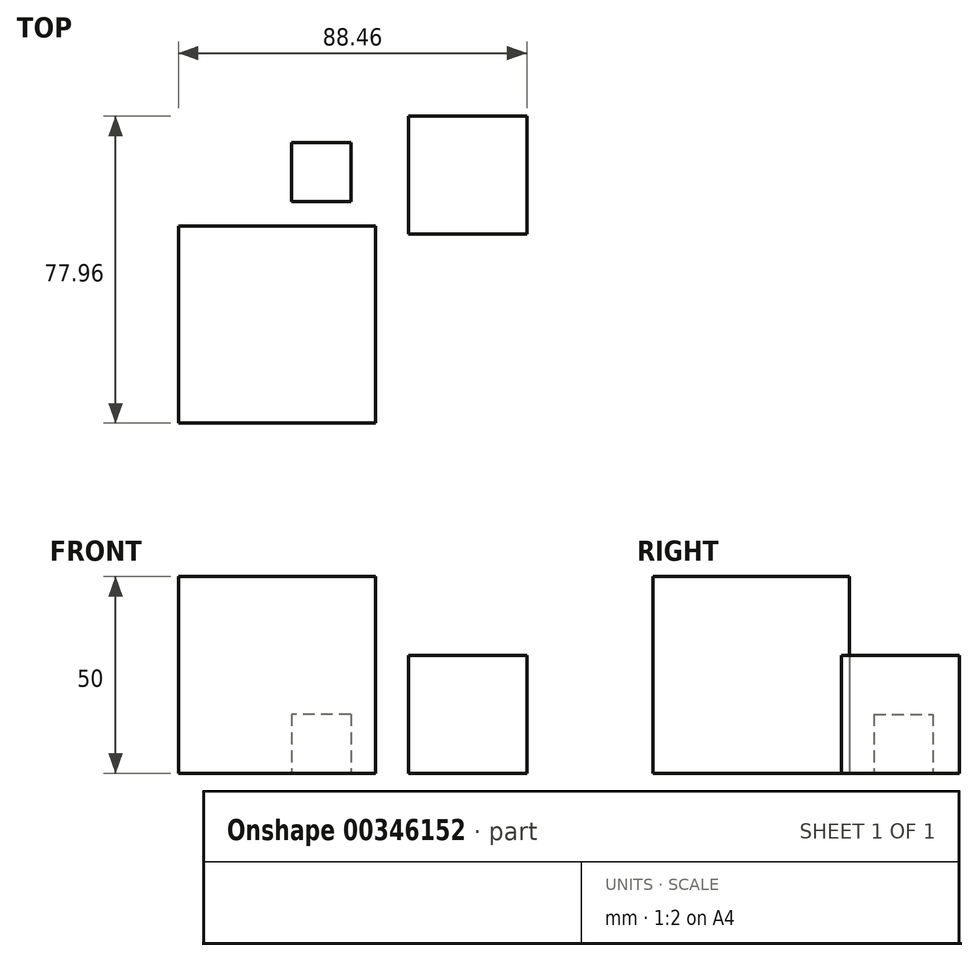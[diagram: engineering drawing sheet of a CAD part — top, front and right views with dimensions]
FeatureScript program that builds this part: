
annotation { "Feature Type Name" : "Feature", "Feature Type Description" : "" }
export const myFeature = defineFeature(function(context is Context, id is Id, definition is map)
    precondition{}
    {
        {
            assignVariable(context, id + "F0", {"name" : "a", "anyValue" : 15});
        }
        {
            assignVariable(context, id + "F1", {"name" : "b", "anyValue" : 30});
        }
        {
            assignVariable(context, id + "F2", {"name" : "c", "anyValue" : 50});
        }
        {
            var Q0;
            Q0=qCreatedBy(makeId("Top.planeOp"),FACE);
            var sketch = newSketch(context, id + "F3", { "sketchPlane" : qUnion([Q0])});
            skLineSegment(sketch, "E0.bottom", {"start": v(-35.32, 58.54) * mm, "end": v(-50.32, 58.54) * mm});
            skLineSegment(sketch, "E0.top", {"start": v(-35.32, 73.54) * mm, "end": v(-50.32, 73.54) * mm});
            skLineSegment(sketch, "E0.left", {"start": v(-35.32, 58.54) * mm, "end": v(-35.32, 73.54) * mm});
            skLineSegment(sketch, "E0.right", {"start": v(-50.32, 58.54) * mm, "end": v(-50.32, 73.54) * mm});
            skLineSegment(sketch, "E1.bottom", {"start": v(-20.62, 50.29) * mm, "end": v(9.38, 50.29) * mm});
            skLineSegment(sketch, "E1.top", {"start": v(-20.62, 80.29) * mm, "end": v(9.38, 80.29) * mm});
            skLineSegment(sketch, "E1.left", {"start": v(-20.62, 50.29) * mm, "end": v(-20.62, 80.29) * mm});
            skLineSegment(sketch, "E1.right", {"start": v(9.38, 50.29) * mm, "end": v(9.38, 80.29) * mm});
            skLineSegment(sketch, "E2.bottom", {"start": v(-79.08, 2.33) * mm, "end": v(-29.08, 2.33) * mm});
            skLineSegment(sketch, "E2.top", {"start": v(-79.08, 52.33) * mm, "end": v(-29.08, 52.33) * mm});
            skLineSegment(sketch, "E2.left", {"start": v(-79.08, 2.33) * mm, "end": v(-79.08, 52.33) * mm});
            skLineSegment(sketch, "E2.right", {"start": v(-29.08, 2.33) * mm, "end": v(-29.08, 52.33) * mm});
            skSolve(sketch);
        }
        {
            var Q0;
            Q0=makeQuery(id+"F3.imprint","IMPRINT",FACE,{"disambiguationData":[TD([[makeQuery(id+"F3.imprint","IMPRINT",EDGE,{"derivedFrom":sQuery(id+"F3.wireOp",EDGE,"E0.bottom")}),-1.0]])]});
            extrude(context, id + "F4", {"entities" : qUnion([Q0]), "depth" : (getVariable(context, 'a')) * mm});
        }
        {
            var Q0;
            Q0=makeQuery(id+"F3.imprint","IMPRINT",FACE,{"disambiguationData":[TD([[makeQuery(id+"F3.imprint","IMPRINT",EDGE,{"derivedFrom":sQuery(id+"F3.wireOp",EDGE,"E2.bottom")}),1.0]])]});
            extrude(context, id + "F5", {"entities" : qUnion([Q0]), "depth" : (getVariable(context, 'c')) * mm});
        }
        {
            var Q0;
            Q0=makeQuery(id+"F3.imprint","IMPRINT",FACE,{"disambiguationData":[TD([[makeQuery(id+"F3.imprint","IMPRINT",EDGE,{"derivedFrom":sQuery(id+"F3.wireOp",EDGE,"E1.top")}),-1.0]])]});
            extrude(context, id + "F6", {"entities" : qUnion([Q0]), "depth" : (getVariable(context, 'b')) * mm});
        }
    });
